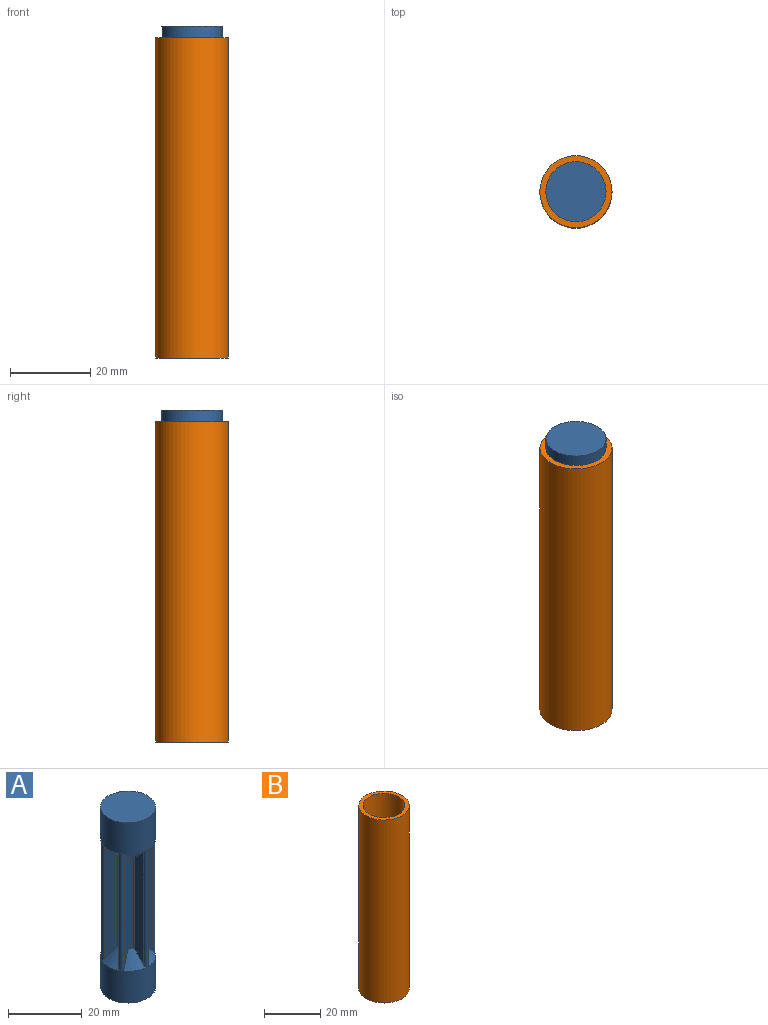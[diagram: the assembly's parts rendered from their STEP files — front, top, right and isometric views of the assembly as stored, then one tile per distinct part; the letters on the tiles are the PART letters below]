
ASSEMBLY  parts=2 mates=1
PART A: 52 faces, bbox 15.2x15.2x60.2 mm
  f0: cylinder r=0.75mm len=31.04mm, axis (0,0,-1), area 26.5mm2, adj f14,f25,f43,f50
  f1: cylinder r=0.75mm len=31.04mm, axis (0,0,-1), area 26.5mm2, adj f14,f23,f43,f50
  f2: cylinder r=0.75mm len=31.04mm, axis (0,0,-1), area 26.5mm2, adj f17,f24,f42,f49
  f3: cylinder r=0.75mm len=31.04mm, axis (0,0,-1), area 26.5mm2, adj f15,f22,f41,f48
  f4: cylinder r=0.75mm len=31.04mm, axis (0,0,-1), area 26.5mm2, adj f17,f19,f42,f49
  f5: cylinder r=0.75mm len=31.04mm, axis (0,0,-1), area 26.5mm2, adj f15,f21,f41,f48
  f6: cylinder r=0.75mm len=31.04mm, axis (0,0,-1), area 26.5mm2, adj f16,f18,f40,f47
  f7: cylinder r=0.75mm len=31.04mm, axis (0,0,-1), area 26.5mm2, adj f13,f20,f39,f46
  f8: cylinder r=0.75mm len=31.04mm, axis (0,0,-1), area 26.5mm2, adj f16,f28,f40,f47
  f9: cylinder r=0.75mm len=31.04mm, axis (0,0,-1), area 26.5mm2, adj f13,f27,f39,f46
  f10: cylinder r=0.75mm len=31.04mm, axis (0,0,-1), area 26.5mm2, adj f12,f29,f38,f45
  f11: cylinder r=0.75mm len=31.04mm, axis (0,0,-1), area 26.5mm2, adj f12,f26,f38,f45
  f12: cylinder r=3mm len=30mm, axis (0,0,-1), area 20.2mm2, adj f10,f11,f38,f45
  f13: cylinder r=3mm len=30mm, axis (0,0,-1), area 20.2mm2, adj f7,f9,f39,f46
  f14: cylinder r=3mm len=30mm, axis (0,0,-1), area 20.2mm2, adj f0,f1,f43,f50
  f15: cylinder r=3mm len=30mm, axis (0,0,-1), area 20.2mm2, adj f3,f5,f41,f48
  f16: cylinder r=3mm len=30mm, axis (0,0,-1), area 20.2mm2, adj f6,f8,f40,f47
  f17: cylinder r=3mm len=30mm, axis (0,0,-1), area 20.2mm2, adj f2,f4,f42,f49
  f18: plane 37.75x3.48mm, normal (-1,0,0), area 113.6mm2, adj f6,f32,f40,f47
  f19: plane 37.75x3.48mm, normal (1,0,0), area 113.6mm2, adj f4,f32,f42,f49
  f20: plane 37.75x3.48mm, normal (-1,0,0), area 113.6mm2, adj f7,f33,f39,f46
  f21: plane 37.75x3.48mm, normal (1,0,0), area 113.6mm2, adj f5,f33,f41,f48
  f22: plane 37.75x3.04mm, normal (-0.5,-0.87,0), area 113.6mm2, adj f3,f31,f41,f48
  f23: plane 37.75x3.04mm, normal (0.5,0.87,0), area 113.6mm2, adj f1,f31,f43,f50
  f24: plane 37.75x3.04mm, normal (-0.5,0.87,0), area 113.6mm2, adj f2,f30,f42,f49
  f25: plane 37.75x3.04mm, normal (0.5,-0.87,0), area 113.6mm2, adj f0,f30,f43,f50
  f26: plane 37.75x3.04mm, normal (-0.5,0.87,0), area 113.6mm2, adj f11,f35,f38,f45
  f27: plane 37.75x3.04mm, normal (0.5,-0.87,0), area 113.6mm2, adj f9,f35,f39,f46
  f28: plane 37.75x3.04mm, normal (0.5,0.87,0), area 113.6mm2, adj f8,f34,f40,f47
  f29: plane 37.75x3.04mm, normal (-0.5,-0.87,0), area 113.6mm2, adj f10,f34,f38,f45
  f30: cylinder r=0.75mm len=39mm, axis (0,0,1), area 90.2mm2, adj f24,f25,f42,f43,f49,f50
  f31: cylinder r=0.75mm len=39mm, axis (0,0,-1), area 90.2mm2, adj f22,f23,f41,f43,f48,f50
  f32: cylinder r=0.75mm len=39mm, axis (0,0,1), area 90.2mm2, adj f18,f19,f40,f42,f47,f49
  f33: cylinder r=0.75mm len=39mm, axis (0,0,-1), area 90.2mm2, adj f20,f21,f39,f41,f46,f48
  f34: cylinder r=0.75mm len=39mm, axis (0,0,1), area 90.2mm2, adj f28,f29,f38,f40,f45,f47
  f35: cylinder r=0.75mm len=39mm, axis (0,0,-1), area 90.2mm2, adj f26,f27,f38,f39,f45,f46
  f36: cylinder r=7.5mm len=15mm, axis (0,0,1), area 494.8mm2, adj f37,f38,f39,f40,f41,f42,f43
  f37: plane 15x15mm, normal (0,0,1), area 176.7mm2, adj f36
  f38: cone r=7.5mm half-angle=45deg, axis (0,0,1), area 25.2mm2, adj f10,f11,f12,f26,f29,f34,f35,f36
  f39: cone r=7.5mm half-angle=45deg, axis (0,0,1), area 25.2mm2, adj f7,f9,f13,f20,f27,f33,f35,f36
  f40: cone r=7.5mm half-angle=45deg, axis (0,0,1), area 25.2mm2, adj f6,f8,f16,f18,f28,f32,f34,f36
  f41: cone r=7.5mm half-angle=45deg, axis (0,0,1), area 25.2mm2, adj f3,f5,f15,f21,f22,f31,f33,f36
  f42: cone r=7.5mm half-angle=45deg, axis (0,0,1), area 25.2mm2, adj f2,f4,f17,f19,f24,f30,f32,f36
  f43: cone r=7.5mm half-angle=45deg, axis (0,0,1), area 25.2mm2, adj f0,f1,f14,f23,f25,f30,f31,f36
  f44: cylinder r=7.5mm len=15mm, axis (0,0,-1), area 494.8mm2, adj f45,f46,f47,f48,f49,f50,f51
  f45: cone r=7.5mm half-angle=45deg, axis (0,0,-1), area 25.2mm2, adj f10,f11,f12,f26,f29,f34,f35,f44
  f46: cone r=7.5mm half-angle=45deg, axis (0,0,-1), area 25.2mm2, adj f7,f9,f13,f20,f27,f33,f35,f44
  f47: cone r=7.5mm half-angle=45deg, axis (0,0,-1), area 25.2mm2, adj f6,f8,f16,f18,f28,f32,f34,f44
  f48: cone r=7.5mm half-angle=45deg, axis (0,0,-1), area 25.2mm2, adj f3,f5,f15,f21,f22,f31,f33,f44
  f49: cone r=7.5mm half-angle=45deg, axis (0,0,-1), area 25.2mm2, adj f2,f4,f17,f19,f24,f30,f32,f44
  f50: cone r=7.5mm half-angle=45deg, axis (0,0,-1), area 25.2mm2, adj f0,f1,f14,f23,f25,f30,f31,f44
  f51: plane 15x15mm, normal (0,0,-1), area 176.7mm2, adj f44
PART B: 4 faces, bbox 18x18x80 mm
  f0: cylinder r=7.5mm len=80mm, axis (0,0,-1), area 3769.9mm2, adj f2,f3
  f1: cylinder r=9mm len=80mm, axis (0,0,-1), area 4523.9mm2, adj f2,f3
  f2: plane 18x18mm, normal (0,0,1), area 77.8mm2, adj f0,f1
  f3: plane 18x18mm, normal (0,0,-1), area 77.8mm2, adj f0,f1
PLACE A t=(17.78,33.91,12.42)mm
PLACE B t=(17.78,33.91,-40.47)mm fixed
MATE slider A.f36 <-> B.f0  axis (0,0,-1) through (17.78,33.91,-17.58)mm
